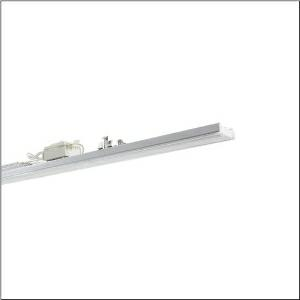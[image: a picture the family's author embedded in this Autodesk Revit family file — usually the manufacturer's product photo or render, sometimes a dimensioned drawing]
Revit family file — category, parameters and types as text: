
# Revit family: licross_r__21_recessed_mo_52te14dv4exg_6364
name_source: partatom
category: Lighting Fixtures
units: mm (PartAtom-declared; Revit-internal decimal feet)

## family parameters
Cut with Voids When Loaded = No
Host = Face
Light Source = No
Part Type = Normal
Room Calculation Point = No
Round Connector Dimension = Use Diameter
Shared = No

## types (1)
- --- (1 x LED, 14200 lm, 85.3 W, 4000K)
    Apparent Load = 85 VA
    CIE Flux Codes = 56 84 97 100 100
    Color Rendering = 80
    Color Temperature = 4000K
    Default Elevation = 1800 mm
    Description = Licross® 21 Recessed MO, luminaire insert, of sheet steel, galvanised, coil coated, white, length: 2.250mm, width: 66mm, height: 67mm, LED rated luminous flux: 14.200lm, light colour: 840, control gear: DALI 2, with plug, 5-pole, with phase selection, mains connection: 220..240V, AC, 50/60Hz, rated input power: 85W, halogen-free wiring, primary light control with lens, of plastic, primary optical cover: cover, of PMMA, light emission: direct distribution, primary light characteristic: asymmetric, protection rating (complete): IP54, insulation class (complete): insulation class I (protective earthing), certification: CE, ENEC, VDE, UKCA, protection symbol: D if used in an environment with non-conductive dust loads with corresponding accessories, impact resistance: IK06, permissible ambient temperature for indoor applications: -25..+35°C, corresponds to IFS (International Featured Standards) requirements for safety and quality in the food industry, reducing of maximum allowable ambient temperature of 5°C with ceiling mounting, LABS conformity tested according to VDMA 24364:2018-05, packaging unit: 1 piece
    Height = 58 mm
    Lamp = 1 x LED
    Lamp Light Flux = 14200 lm
    Lamp Power = 85.3 W
    Lamp count = 1
    Length = 2250 mm
    Luminous efficacy = 166 lm/W
    Manufacturer = Siteco
    ModVariant = No
    Model = 52TE14DV4EXG
    Mounting Place = Ceiling
    Mounting Type = Pendant
    Number of Poles = 1
    OnlyDefault = Yes
    Power Factor = 1
    Product Name = Licross® 21 Recessed MO
    Product group = luminaire insert
    ProductGroupID = 902
    Protection Class = Protection class I
    Protection Degree = IP 54
    RLX_Detail_Level = 1
    RLX_Emergency_Light_Flux = 0 lm
    RLX_Emergency_Type = 0
    RLX_Emergency_Type_DB = No
    RlxData = <blob elided: 30061 chars, md5=6e4729db>
    Socket = socket
    Standby Power = 0 W
    System Light Flux = 14200 lm
    System Power = 85 W
    Type Comments = factory setting: luminous flux: 100 % | dim-lin: 254 | 390 mA
    Type Image = l_1296930.jpg
    URL = http://relux.com
    VarID = @adj_127800
    Voltage = 0 V
    Weight = 0.00 kg
    Width = 66 mm

## geometry (parser evidence)
native form markers: Blend x4, Sweep x10
no freeform markers — native parametric forms only
